# Revit family: Indoor_Table Lamp_Santa&Cole_TMD
name_source: partatom
category: Luminarias
revit_build: Autodesk Revit 2018 (Build: 20190510_1515(x64)
units: mm (PartAtom-declared; Revit-internal decimal feet)

## family parameters
Compartido = No
Corte con vacíos al cargar = No
Cota de conector redondo = Diámetro de uso
Número OmniClass = 23.80.70.00
Origen de luz = Sí
Punto de cálculo de habitación = No
Se basa en plano de trabajo = No
Siempre vertical = Sí
Tipo de pieza = Normal
Título OmniClass = Lighting

## types (1)
- Indoor_Table Lamp_Santa&Cole_TMD
    Assembly instructions - CE = https://www.santacole.com
    Assembly instructions - UL = https://www.santacole.com
    Cambio de temperatura de color de luz atenuada = <Ninguno>
    Carga aparente = 5 VA
    Code = TME08
    Energy Label = https://www.santacole.com
    Fabricante = Santa & Cole
    Filtro de color = 16777215
    Load = 5 W
    Manufacturer website = http://www.santacole.com
    Modelo = TMD
    Tamaño de símbolo de origen de luz = 50 mm  [stored 0.164042 ft]
    Technical Information = https://www.santacole.com
    URL = https://www.santacole.com

note: [stored X ft] marks values corroborated as IEEE doubles in the binary element streams (Revit-internal decimal feet)
